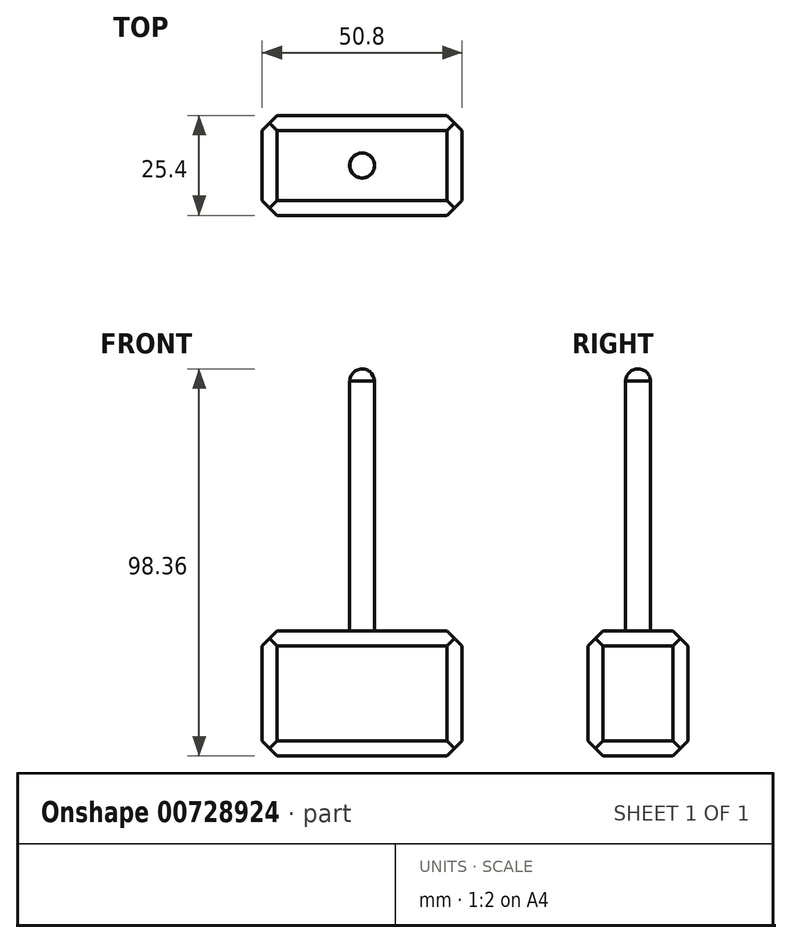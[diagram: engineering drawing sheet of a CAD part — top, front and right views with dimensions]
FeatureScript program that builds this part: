
annotation { "Feature Type Name" : "Feature", "Feature Type Description" : "" }
export const myFeature = defineFeature(function(context is Context, id is Id, definition is map)
    precondition{}
    {
        {
            var Q0;
            Q0=qCreatedBy(makeId("Top.planeOp"),FACE);
            var sketch = newSketch(context, id + "F0", { "sketchPlane" : qUnion([Q0])});
            skLineSegment(sketch, "E0.bottom", {"start": v(25.4, -12.7) * mm, "end": v(-25.4, -12.7) * mm});
            skLineSegment(sketch, "E0.top", {"start": v(25.4, 12.7) * mm, "end": v(-25.4, 12.7) * mm});
            skLineSegment(sketch, "E0.left", {"start": v(25.4, -12.7) * mm, "end": v(25.4, 12.7) * mm});
            skLineSegment(sketch, "E0.right", {"start": v(-25.4, -12.7) * mm, "end": v(-25.4, 12.7) * mm});
            skPoint(sketch, "E0.middle", {"position": v(0, 0) * mm});
            skSolve(sketch);
        }
        {
            var Q0;
            Q0 = qSketchRegion(id + "F0", true);
            extrude(context, id + "F1", {"entities" : qUnion([Q0]), "depth" : 31.75 * mm, "offsetDistance" : 25.4 * mm});
        }
        {
            var Q0;
            Q0=makeQuery(id+"F1.opExtrude","CAP_FACE",FACE,{"disambiguationData":[OSD([sQuery(id+"F0.wireOp",EDGE,"E0.bottom"),sQuery(id+"F0.wireOp",EDGE,"E0.top"),sQuery(id+"F0.wireOp",EDGE,"E0.left"),sQuery(id+"F0.wireOp",EDGE,"E0.right")])],"isStart":false});
            var sketch = newSketch(context, id + "F2", { "sketchPlane" : qUnion([Q0])});
            skCircle(sketch, "E1", {"center": v(0, 0) * mm, "radius": 3.18 * mm});
            skSolve(sketch);
        }
        {
            var Q0;
            Q0=makeQuery(id+"F2.imprint","IMPRINT",FACE,{"disambiguationData":[TD([[makeQuery(id+"F2.imprint","IMPRINT",EDGE,{"derivedFrom":sQuery(id+"F2.wireOp",EDGE,"E1")}),1.0]])]});
            extrude(context, id + "F3", {"entities" : qUnion([Q0]), "operationType" : NewBodyOperationType.ADD, "depth" : 63.5 * mm, "offsetDistance" : 25.4 * mm});
        }
        {
            var Q0;
            Q0=makeQuery(id+"F1.opExtrude","CAP_EDGE",EDGE,{"disambiguationData":[OSD([sQuery(id+"F0.wireOp",EDGE,"E0.bottom")])],"isStart":true});
            var Q1;
            Q1=makeQuery(id+"F1.opExtrude","CAP_EDGE",EDGE,{"disambiguationData":[OSD([sQuery(id+"F0.wireOp",EDGE,"E0.top")])],"isStart":true});
            var Q2;
            Q2=makeQuery(id+"F1.opExtrude","CAP_EDGE",EDGE,{"disambiguationData":[OSD([sQuery(id+"F0.wireOp",EDGE,"E0.top")])],"isStart":false});
            var Q3;
            Q3=makeQuery(id+"F1.opExtrude","CAP_EDGE",EDGE,{"disambiguationData":[OSD([sQuery(id+"F0.wireOp",EDGE,"E0.bottom")])],"isStart":false});
            var Q4;
            Q4=makeQuery(id+"F1.opExtrude","CAP_EDGE",EDGE,{"disambiguationData":[OSD([sQuery(id+"F0.wireOp",EDGE,"E0.right")])],"isStart":false});
            var Q5;
            Q5=makeQuery(id+"F1.opExtrude","CAP_EDGE",EDGE,{"disambiguationData":[OSD([sQuery(id+"F0.wireOp",EDGE,"E0.right")])],"isStart":true});
            var Q6;
            Q6=makeQuery(id+"F1.opExtrude","CAP_EDGE",EDGE,{"disambiguationData":[OSD([sQuery(id+"F0.wireOp",EDGE,"E0.left")])],"isStart":true});
            chamfer(context, id + "F4", {"entities" : qUnion([Q0, Q1, Q2, Q3, Q4, Q5, Q6]), "width" : 3.8 * mm, "tangentPropagation" : true});
        }
        {
            var Q0;
            Q0=makeQuery(id+"F1.opExtrude","SWEPT_EDGE",EDGE,{"disambiguationData":[OSD([sQuery(id+"F0.wireOp",EDGE,"E0.bottom"),sQuery(id+"F0.wireOp",EDGE,"E0.left")])]});
            var Q1;
            Q1=makeQuery(id+"F1.opExtrude","SWEPT_EDGE",EDGE,{"disambiguationData":[OSD([sQuery(id+"F0.wireOp",EDGE,"E0.top"),sQuery(id+"F0.wireOp",EDGE,"E0.right")])]});
            var Q2;
            Q2=makeQuery(id+"F1.opExtrude","SWEPT_EDGE",EDGE,{"disambiguationData":[OSD([sQuery(id+"F0.wireOp",EDGE,"E0.top"),sQuery(id+"F0.wireOp",EDGE,"E0.left")])]});
            var Q3;
            Q3=makeQuery(id+"F1.opExtrude","SWEPT_EDGE",EDGE,{"disambiguationData":[OSD([sQuery(id+"F0.wireOp",EDGE,"E0.bottom"),sQuery(id+"F0.wireOp",EDGE,"E0.right")])]});
            chamfer(context, id + "F5", {"entities" : qUnion([Q0, Q1, Q2, Q3]), "width" : 3.8 * mm, "tangentPropagation" : true});
        }
        {
            var Q0;
            Q0=makeQuery(id+"F1.opExtrude","CAP_EDGE",EDGE,{"disambiguationData":[OSD([sQuery(id+"F0.wireOp",EDGE,"E0.left")])],"isStart":false});
            chamfer(context, id + "F6", {"entities" : qUnion([Q0]), "width" : 3.8 * mm, "tangentPropagation" : true});
        }
        {
            var Q0;
            Q0=makeQuery(id+"F3.opExtrude","CAP_FACE",FACE,{"disambiguationData":[OSD([sQuery(id+"F2.wireOp",EDGE,"E1")])],"isStart":false});
            var sketch = newSketch(context, id + "F7", { "sketchPlane" : qUnion([Q0])});
            skArc(sketch, "E2", {"start": v(0, -3.18) * mm, "mid": v(3.11, 0) * mm, "end": v(0, 3.18) * mm});
            skLineSegment(sketch, "E3", {"start": v(0, 3.18) * mm, "end": v(0, -3.18) * mm});
            skSolve(sketch);
        }
        {
            var Q0;
            Q0=makeQuery(id+"F7.imprint","IMPRINT",FACE,{"disambiguationData":[TD([[makeQuery(id+"F7.imprint","IMPRINT",EDGE,{"derivedFrom":sQuery(id+"F7.wireOp",EDGE,"E2")}),1.0]])]});
            var Q1;
            Q1=sQuery(id+"F7.wireOp",EDGE,"E3");
            revolve(context, id + "F8", {"operationType" : NewBodyOperationType.ADD, "surfaceOperationType" : NewSurfaceOperationType.NEW, "entities" : qUnion([Q0]), "axis" : qUnion([Q1]), "revolveType" : RevolveType.FULL});
        }
    });
